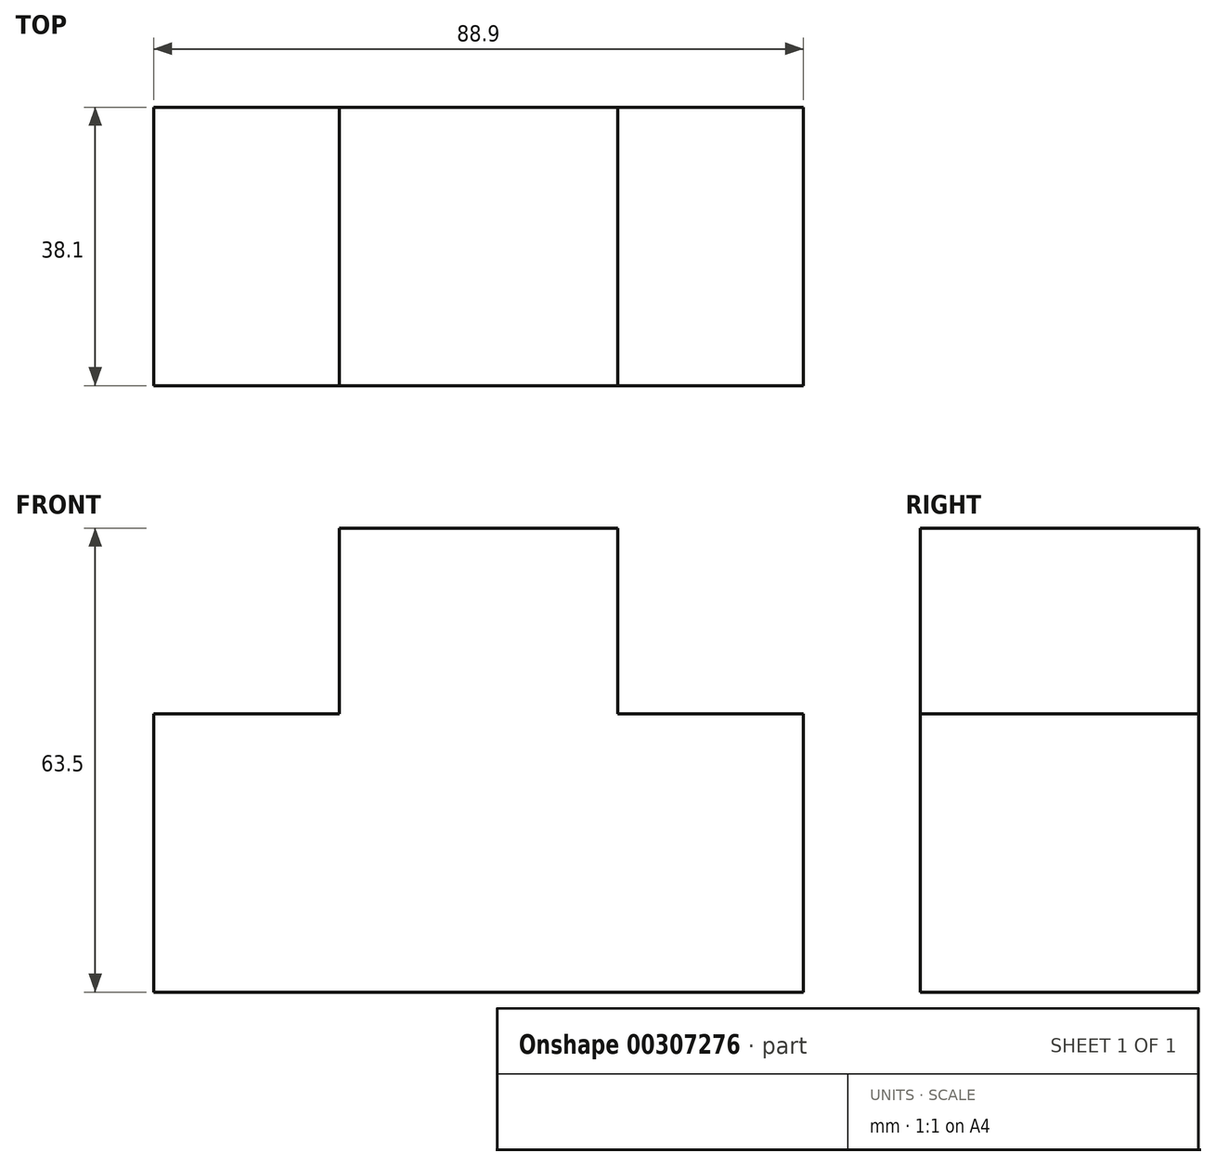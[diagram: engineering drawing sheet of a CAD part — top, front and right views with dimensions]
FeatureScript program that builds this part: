
annotation { "Feature Type Name" : "Feature", "Feature Type Description" : "" }
export const myFeature = defineFeature(function(context is Context, id is Id, definition is map)
    precondition{}
    {
        {
            var Q0;
            Q0=qCreatedBy(makeId("Front.planeOp"),FACE);
            var sketch = newSketch(context, id + "F0", { "sketchPlane" : qUnion([Q0])});
            skLineSegment(sketch, "E0", {"start": v(-43.11, -47.77) * mm, "end": v(45.79, -47.77) * mm});
            skLineSegment(sketch, "E1", {"start": v(45.79, -47.77) * mm, "end": v(45.79, -9.67) * mm});
            skLineSegment(sketch, "E2", {"start": v(45.79, -9.67) * mm, "end": v(20.39, -9.67) * mm});
            skLineSegment(sketch, "E3", {"start": v(20.39, -9.67) * mm, "end": v(20.39, 15.73) * mm});
            skLineSegment(sketch, "E4", {"start": v(20.39, 15.73) * mm, "end": v(-17.71, 15.73) * mm});
            skLineSegment(sketch, "E5", {"start": v(-17.71, 15.73) * mm, "end": v(-17.71, -9.67) * mm});
            skLineSegment(sketch, "E6", {"start": v(-17.71, -9.67) * mm, "end": v(-43.11, -9.67) * mm});
            skLineSegment(sketch, "E7", {"start": v(-43.11, -9.67) * mm, "end": v(-43.11, -47.77) * mm});
            skSolve(sketch);
        }
        {
            var Q0;
            Q0=makeQuery(id+"F0.imprint","IMPRINT",FACE,{"disambiguationData":[TD([[makeQuery(id+"F0.imprint","IMPRINT",EDGE,{"derivedFrom":sQuery(id+"F0.wireOp",EDGE,"E0")}),1.0]])]});
            extrude(context, id + "F1", {"entities" : qUnion([Q0]), "depth" : 38.1 * mm});
        }
    });
